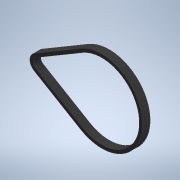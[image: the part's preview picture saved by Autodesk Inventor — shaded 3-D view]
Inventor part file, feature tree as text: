
AUTODESK INVENTOR PART (.ipt)
format: ipt  version: 2020 (Build 240168000, 168)  size: 117,760 bytes
history: native  units: in
note: dims shown in document units (in); Inventor stores cm internally (conversion verified against a paired STEP export)
features: extrude x1, sketch x1
ambient origin geometry x8: Origin, YZ Plane, XZ Plane, XY Plane, X Axis, Y Axis, Z Axis, Center Point
bodies: Solid1 (feature_tree)
feature tree (2):
  extrude  "Extrusion1"  Depth=0.15in
  sketch  "Sketch1"  dims[d0=0.752in d1=3.7594in d2=2.9547in d4=0.3543in d5=0.0in d6=0.1159in d7=0.15in]
